FCSTD DOCUMENT  (FreeCAD 0.19R)
Label: BeltDriveUnit
License: All rights reserved
LicenseURL: http://en.wikipedia.org/wiki/All_rights_reserved
objects: Sketcher::SketchObject×1, PartDesign::Body×1
note: 2 computed .brp shape members not serialized (recipe doc carries the construction recipe); baked Part::Feature solids carry a one-line shape summary decoded from their .brp

FEATURE [Sketcher::SketchObject] Sketch
  FullyConstrained = false
  MapMode = 5
  Support = -> [XY_Plane]
  sketch-geometry (20):
    g0: LineSegment StartX=-30 StartY=29 StartZ=0 EndX=343.79 EndY=29 EndZ=0
    g1: LineSegment StartX=343.79 StartY=29 StartZ=0 EndX=343.79 EndY=9 EndZ=0
    g2: LineSegment StartX=343.79 StartY=9 StartZ=0 EndX=-30 EndY=9 EndZ=0
    g3: LineSegment StartX=-30 StartY=9 StartZ=0 EndX=-30 EndY=29 EndZ=0
    g4: Circle CenterX=0 CenterY=0 CenterZ=0 NormalX=0 NormalY=0 NormalZ=1 AngleXU=0 Radius=8.5
    g5: LineSegment StartX=40 StartY=-150 StartZ=0 EndX=40 EndY=150 EndZ=0
    g6: Circle CenterX=-0.502057 CenterY=-0.280385 CenterZ=0 NormalX=0 NormalY=0 NormalZ=1 AngleXU=0 Radius=27
    g7: LineSegment StartX=-6.09661 StartY=-27.8704 StartZ=0 EndX=33.9034 EndY=-27.8704 EndZ=0
    g8: LineSegment StartX=33.9034 StartY=-27.8704 StartZ=0 EndX=33.9034 EndY=-67.8704 EndZ=0
    g9: LineSegment StartX=33.9034 StartY=-67.8704 StartZ=0 EndX=-6.09661 EndY=-67.8704 EndZ=0
    g10: LineSegment StartX=-6.09661 StartY=-67.8704 StartZ=0 EndX=-6.09661 EndY=-27.8704 EndZ=0
    g11: Circle CenterX=13.9034 CenterY=-47.8704 CenterZ=0 NormalX=0 NormalY=0 NormalZ=1 AngleXU=0 Radius=8.39
    g12: LineSegment StartX=2 StartY=32 StartZ=0 EndX=42 EndY=32 EndZ=0
    g13: LineSegment StartX=2 StartY=32 StartZ=0 EndX=2 EndY=52 EndZ=0
    g14: LineSegment StartX=2 StartY=52 StartZ=0 EndX=42 EndY=52 EndZ=0
    g15: LineSegment StartX=42 StartY=52 StartZ=0 EndX=42 EndY=32 EndZ=0
    g16: LineSegment StartX=-22 StartY=45 StartZ=0 EndX=-3.46 EndY=45 EndZ=0
    g17: LineSegment StartX=-3.46 StartY=45 StartZ=0 EndX=-3.46 EndY=39 EndZ=0
    g18: LineSegment StartX=-3.46 StartY=39 StartZ=0 EndX=-22 EndY=39 EndZ=0
    g19: LineSegment StartX=-22 StartY=39 StartZ=0 EndX=-22 EndY=45 EndZ=0
  constraints (54):
    c: Coincident(g1,g2)
    c: Coincident(g2,g3)
    c: Coincident(g3,g0)
    c: Horizontal(g0)
    c: Horizontal(g2)
    c: Vertical(g1)
    c: Vertical(g3)
    c: Distance(g3) = 20
    c: Diameter(g4) = 17
    c: Coincident(g4,g-1)
    c: DistanceX(g5) = 40
    c: DistanceY(g2) = 9
    c: Distance(g5) = 300
    c: Symmetric(g5,g5,g-1)
    c: Coincident(g0,g1)
    c: Distance(g0) = 373.79
    c: Diameter(g6) = 54
    c: Coincident(g7,g8)
    c: Coincident(g8,g9)
    c: Coincident(g9,g10)
    c: Coincident(g10,g7)
    c: Horizontal(g7)
    c: Horizontal(g9)
    c: Vertical(g8)
    c: Vertical(g10)
    c: Equal(g7,g10)
    c: Distance(g7) = 40
    c: Diameter(g11) = 16.78
    c: Symmetric(g7,g9,g11)
    c: Horizontal(g12)
    c: Coincident(g12,g13)
    c: Vertical(g13)
    c: Coincident(g13,g14)
    c: Horizontal(g14)
    c: Coincident(g14,g15)
    c: Coincident(g15,g12)
    c: Vertical(g15)
    c: Distance(g15) = 20
    c: Distance(g14) = 40
    c: Distance(g12,g0) = 3
    c: Coincident(g16,g17)
    c: Coincident(g17,g18)
    c: Coincident(g18,g19)
    c: Coincident(g19,g16)
    c: Horizontal(g16)
    c: Horizontal(g18)
    c: Vertical(g17)
    c: Vertical(g19)
    c: DistanceX(g0,g18) = 8
    c: DistanceX(g2) = -30
    c: Distance(g17) = 6
    c: DistanceY(g12,g17) = 7
    c: Distance(g16) = 18.54
    c: DistanceX(g-1,g12) = 2
FEATURE [PartDesign::Body] Body
  Group = -> [Sketch]
  Origin = -> Origin
